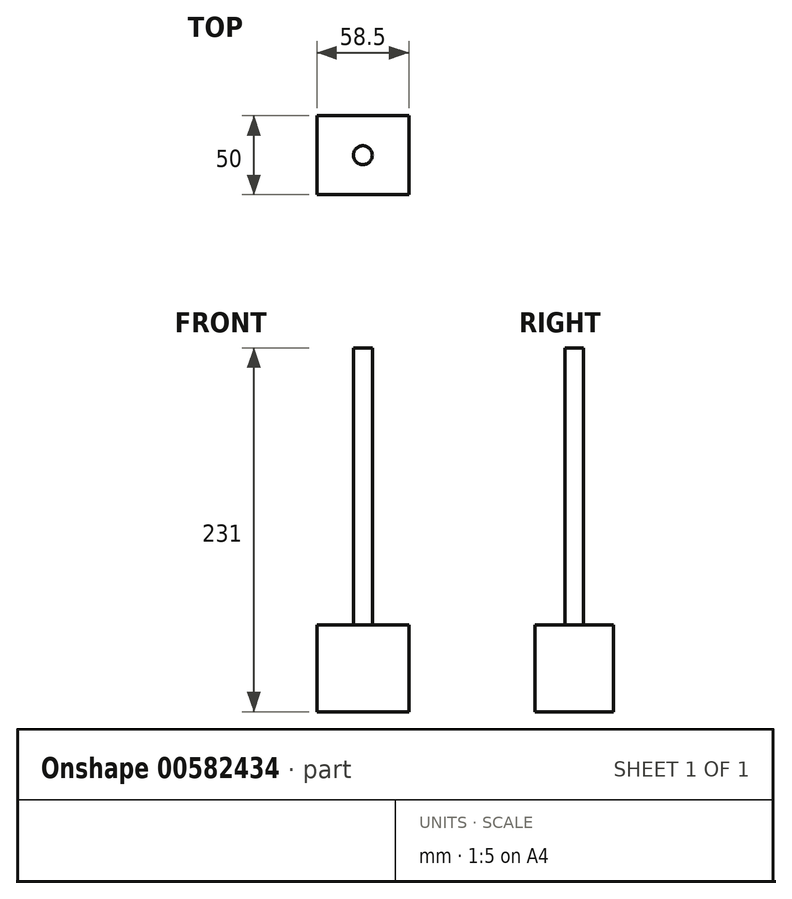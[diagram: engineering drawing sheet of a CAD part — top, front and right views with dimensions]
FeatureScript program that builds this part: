
annotation { "Feature Type Name" : "Feature", "Feature Type Description" : "" }
export const myFeature = defineFeature(function(context is Context, id is Id, definition is map)
    precondition{}
    {
        {
            var Q0;
            Q0=qCreatedBy(makeId("Top.planeOp"),FACE);
            var sketch = newSketch(context, id + "F0", { "sketchPlane" : qUnion([Q0])});
            skLineSegment(sketch, "E0.bottom", {"start": v(0, 0) * mm, "end": v(58.5, 0) * mm});
            skLineSegment(sketch, "E0.top", {"start": v(0, 50) * mm, "end": v(58.5, 50) * mm});
            skLineSegment(sketch, "E0.left", {"start": v(0, 0) * mm, "end": v(0, 50) * mm});
            skLineSegment(sketch, "E0.right", {"start": v(58.5, 0) * mm, "end": v(58.5, 50) * mm});
            skSolve(sketch);
        }
        {
            var Q0;
            Q0 = qSketchRegion(id + "F0", true);
            extrude(context, id + "F1", {"entities" : qUnion([Q0]), "depth" : 55 * mm, "offsetDistance" : 25 * mm});
        }
        {
            var Q0;
            Q0=makeQuery(id+"F1.opExtrude","CAP_FACE",FACE,{"disambiguationData":[OSD([sQuery(id+"F0.wireOp",EDGE,"E0.bottom"),sQuery(id+"F0.wireOp",EDGE,"E0.top"),sQuery(id+"F0.wireOp",EDGE,"E0.left"),sQuery(id+"F0.wireOp",EDGE,"E0.right")])],"isStart":false});
            var sketch = newSketch(context, id + "F2", { "sketchPlane" : qUnion([Q0])});
            skLineSegment(sketch, "E1", {"start": v(0, 50) * mm, "end": v(58.5, 0) * mm, "construction": true});
            skLineSegment(sketch, "E2", {"start": v(0, 0) * mm, "end": v(58.5, 50) * mm, "construction": true});
            skCircle(sketch, "E3", {"center": v(29.25, 25) * mm, "radius": 6 * mm});
            skSolve(sketch);
        }
        {
            var Q0;
            Q0 = qSketchRegion(id + "F2", true);
            extrude(context, id + "F3", {"entities" : qUnion([Q0]), "operationType" : NewBodyOperationType.ADD, "depth" : 176 * mm, "offsetDistance" : 25 * mm});
        }
    });
